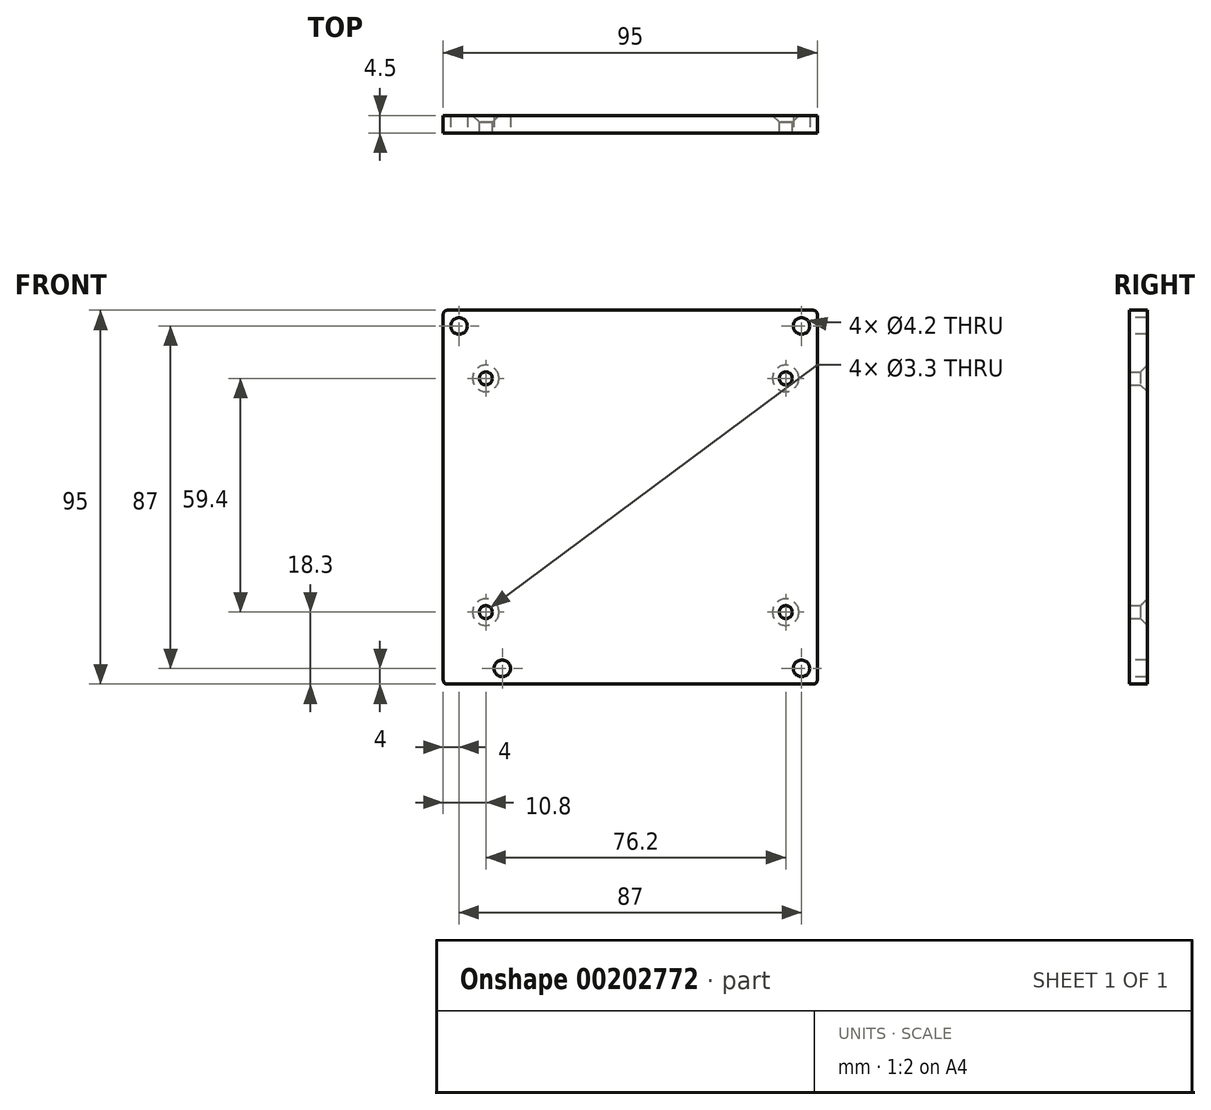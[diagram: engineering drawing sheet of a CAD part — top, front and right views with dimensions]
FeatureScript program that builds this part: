
annotation { "Feature Type Name" : "Feature", "Feature Type Description" : "" }
export const myFeature = defineFeature(function(context is Context, id is Id, definition is map)
    precondition{}
    {
        {
            var Q0;
            Q0=qCreatedBy(makeId("Front.planeOp"),FACE);
            var sketch = newSketch(context, id + "F0", { "sketchPlane" : qUnion([Q0])});
            skLineSegment(sketch, "E0.bottom", {"start": v(47.5, 47.5) * mm, "end": v(-47.5, 47.5) * mm});
            skLineSegment(sketch, "E0.top", {"start": v(47.5, -47.5) * mm, "end": v(-47.5, -47.5) * mm});
            skLineSegment(sketch, "E0.left", {"start": v(47.5, 47.5) * mm, "end": v(47.5, -47.5) * mm});
            skLineSegment(sketch, "E0.right", {"start": v(-47.5, 47.5) * mm, "end": v(-47.5, -47.5) * mm});
            skPoint(sketch, "E0.middle", {"position": v(0, 0) * mm});
            skSolve(sketch);
        }
        {
            var Q0;
            Q0=makeQuery(id+"F0.imprint","IMPRINT",FACE,{"disambiguationData":[TD([[makeQuery(id+"F0.imprint","IMPRINT",EDGE,{"derivedFrom":sQuery(id+"F0.wireOp",EDGE,"E0.bottom")}),1.0]])]});
            extrude(context, id + "F1", {"entities" : qUnion([Q0]), "depth" : 4.5 * mm});
        }
        {
            var Q0;
            Q0=makeQuery(id+"F1.opExtrude","CAP_FACE",FACE,{"disambiguationData":[OSD([sQuery(id+"F0.wireOp",EDGE,"E0.bottom"),sQuery(id+"F0.wireOp",EDGE,"E0.top"),sQuery(id+"F0.wireOp",EDGE,"E0.left"),sQuery(id+"F0.wireOp",EDGE,"E0.right")])],"isStart":false});
            var sketch = newSketch(context, id + "F2", { "sketchPlane" : qUnion([Q0])});
            skCircle(sketch, "E1", {"center": v(43.5, 43.5) * mm, "radius": 2.1 * mm});
            skCircle(sketch, "E2", {"center": v(43.5, -43.5) * mm, "radius": 2.1 * mm});
            skCircle(sketch, "E3", {"center": v(-32.5, -43.5) * mm, "radius": 2.1 * mm});
            skCircle(sketch, "E4", {"center": v(-43.5, 43.5) * mm, "radius": 2.1 * mm});
            skSolve(sketch);
        }
        {
            var Q0;
            Q0 = qSketchRegion(id + "F2", true);
            extrude(context, id + "F3", {"entities" : qUnion([Q0]), "operationType" : NewBodyOperationType.REMOVE, "endBound" : BoundingType.UP_TO_NEXT, "oppositeDirection" : true, "depth" : 25.4 * mm});
        }
        {
            var Q0;
            Q0=makeQuery(id+"F1.opExtrude","SWEPT_EDGE",EDGE,{"disambiguationData":[OSD([sQuery(id+"F0.wireOp",EDGE,"E0.bottom"),sQuery(id+"F0.wireOp",EDGE,"E0.right")])]});
            var Q1;
            Q1=makeQuery(id+"F1.opExtrude","SWEPT_EDGE",EDGE,{"disambiguationData":[OSD([sQuery(id+"F0.wireOp",EDGE,"E0.bottom"),sQuery(id+"F0.wireOp",EDGE,"E0.left")])]});
            var Q2;
            Q2=makeQuery(id+"F1.opExtrude","SWEPT_EDGE",EDGE,{"disambiguationData":[OSD([sQuery(id+"F0.wireOp",EDGE,"E0.top"),sQuery(id+"F0.wireOp",EDGE,"E0.left")])]});
            var Q3;
            Q3=makeQuery(id+"F1.opExtrude","SWEPT_EDGE",EDGE,{"disambiguationData":[OSD([sQuery(id+"F0.wireOp",EDGE,"E0.top"),sQuery(id+"F0.wireOp",EDGE,"E0.right")])]});
            fillet(context, id + "F4", {"entities" : qUnion([Q0, Q1, Q2, Q3]), "radius" : 1 * mm, "tangentPropagation" : true, "allowEdgeOverflow" : false});
        }
        {
            var Q0;
            Q0=makeQuery(id+"F1.opExtrude","CAP_FACE",FACE,{"disambiguationData":[OSD([sQuery(id+"F0.wireOp",EDGE,"E0.bottom"),sQuery(id+"F0.wireOp",EDGE,"E0.top"),sQuery(id+"F0.wireOp",EDGE,"E0.left"),sQuery(id+"F0.wireOp",EDGE,"E0.right")])],"isStart":true});
            var sketch = newSketch(context, id + "F5", { "sketchPlane" : qUnion([Q0])});
            skPoint(sketch, "E5", {"position": v(36.7, 30.2) * mm});
            skPoint(sketch, "E6", {"position": v(36.7, -29.2) * mm});
            skPoint(sketch, "E7", {"position": v(-39.5, -29.2) * mm});
            skPoint(sketch, "E8", {"position": v(-39.5, 30.2) * mm});
            skSolve(sketch);
        }
        {
            var Q0;
            Q0=sQuery(id+"F5.wireOp",VERTEX,"E8");
            var Q1;
            Q1=sQuery(id+"F5.wireOp",VERTEX,"E5");
            var Q2;
            Q2=sQuery(id+"F5.wireOp",VERTEX,"E6");
            var Q3;
            Q3=sQuery(id+"F5.wireOp",VERTEX,"E7");
            var Q4;
            Q4=makeQuery(id+"F1.opExtrude","SWEPT_BODY",BODY,{"disambiguationData":[OSD([sQuery(id+"F0.wireOp",EDGE,"E0.bottom"),sQuery(id+"F0.wireOp",EDGE,"E0.top"),sQuery(id+"F0.wireOp",EDGE,"E0.left"),sQuery(id+"F0.wireOp",EDGE,"E0.right")])]});
            hole(context, id + "F6", {"style" : HoleStyle.C_SINK, "endStyle" : HoleEndStyle.THROUGH, "standardTappedOrClearance" : lookupTablePath({ "standard" : "ISO", "fit" : "Normal", "size" : "M3", "type" : "Clearance" }), "standardBlindInLast" : lookupTablePath({ "fit" : "Standard", "standard" : "ISO", "size" : "M3", "type" : "Clearance" }), "holeDiameter" : 3.3 * mm, "cSinkDiameter" : 6.72 * mm, "cSinkAngle" : 90 * degree, "startFromSketch" : true, "locations" : qUnion([Q0, Q1, Q2, Q3]), "scope" : qUnion([Q4]), "isTappedThrough" : true});
        }
        {
            var Q0;
            Q0=makeQuery(id+"F1.opExtrude","CAP_FACE",FACE,{"disambiguationData":[OSD([sQuery(id+"F0.wireOp",EDGE,"E0.bottom"),sQuery(id+"F0.wireOp",EDGE,"E0.top"),sQuery(id+"F0.wireOp",EDGE,"E0.left"),sQuery(id+"F0.wireOp",EDGE,"E0.right")])],"isStart":false});
            var sketch = newSketch(context, id + "F7", { "sketchPlane" : qUnion([Q0])});
            skPoint(sketch, "E9", {"position": v(0, 31.25) * mm});
            skPoint(sketch, "E10", {"position": v(31.25, 0) * mm});
            skPoint(sketch, "E11", {"position": v(0, -31.25) * mm});
            skPoint(sketch, "E12", {"position": v(-31.25, 0) * mm});
            skPoint(sketch, "E13", {"position": v(-31.25, 31.25) * mm});
            skPoint(sketch, "E14", {"position": v(-31.25, -31.25) * mm});
            skPoint(sketch, "E15", {"position": v(31.25, -31.25) * mm});
            skPoint(sketch, "E16", {"position": v(31.25, 31.25) * mm});
            skSolve(sketch);
        }
    });
